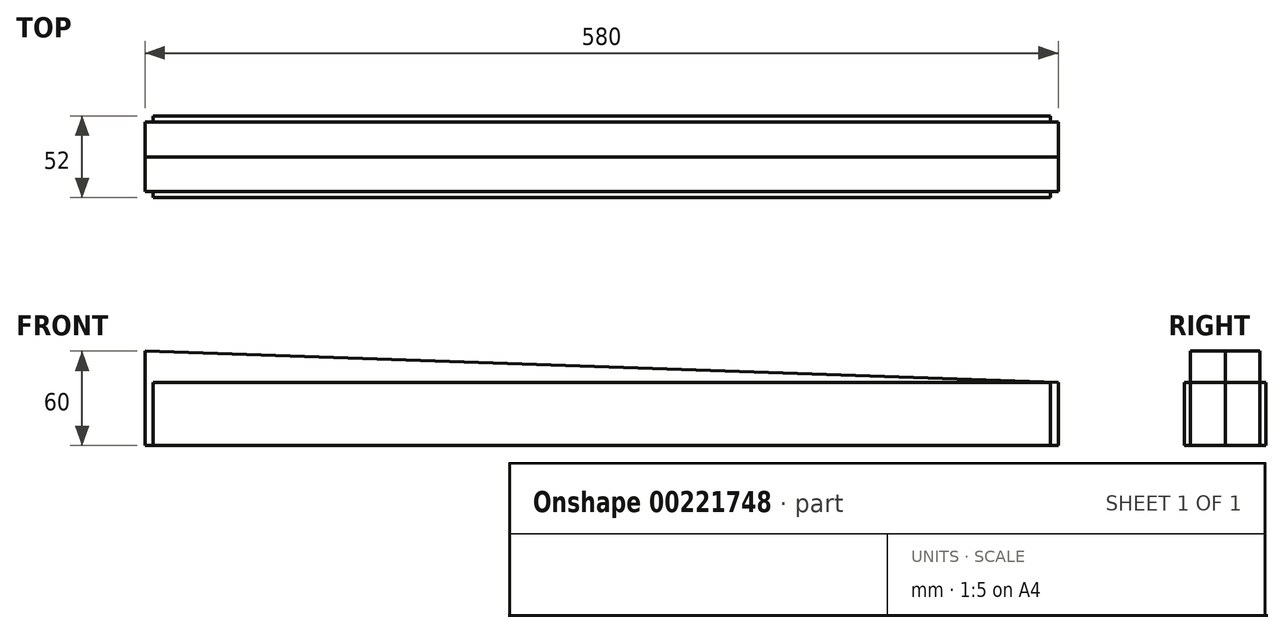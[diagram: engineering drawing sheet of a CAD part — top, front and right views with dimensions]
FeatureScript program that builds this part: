
annotation { "Feature Type Name" : "Feature", "Feature Type Description" : "" }
export const myFeature = defineFeature(function(context is Context, id is Id, definition is map)
    precondition{}
    {
        {
            var Q0;
            Q0=qCreatedBy(makeId("Front.planeOp"),FACE);
            var sketch = newSketch(context, id + "F0", { "sketchPlane" : qUnion([Q0])});
            skLineSegment(sketch, "E0.bottom", {"start": v(-290, 40) * mm, "end": v(290, 20) * mm});
            skLineSegment(sketch, "E0.top", {"start": v(-290, -20) * mm, "end": v(290, -20) * mm});
            skLineSegment(sketch, "E0.left", {"start": v(-290, 40) * mm, "end": v(-290, -20) * mm});
            skLineSegment(sketch, "E0.right", {"start": v(290, 20) * mm, "end": v(290, -20) * mm});
            skPoint(sketch, "E0.middle", {"position": v(0, 0) * mm});
            skSolve(sketch);
        }
        {
            var Q0;
            Q0 = qSketchRegion(id + "F0", true);
            extrude(context, id + "F1", {"entities" : qUnion([Q0]), "depth" : 22 * mm});
        }
        {
            var Q0;
            Q0=makeQuery(id+"F1.opExtrude","CAP_FACE",FACE,{"disambiguationData":[OSD([sQuery(id+"F0.wireOp",EDGE,"E0.bottom"),sQuery(id+"F0.wireOp",EDGE,"E0.top"),sQuery(id+"F0.wireOp",EDGE,"E0.left"),sQuery(id+"F0.wireOp",EDGE,"E0.right")])],"isStart":true});
            var sketch = newSketch(context, id + "F2", { "sketchPlane" : qUnion([Q0])});
            skLineSegment(sketch, "E1.0", {"start": v(290, -20) * mm, "end": v(-290, -20) * mm});
            skLineSegment(sketch, "E2", {"start": v(-285, -20) * mm, "end": v(-285, 20) * mm});
            skLineSegment(sketch, "E3", {"start": v(-285, 20) * mm, "end": v(285, 20) * mm});
            skLineSegment(sketch, "E4", {"start": v(285, 20) * mm, "end": v(285, -20) * mm});
            skSolve(sketch);
        }
        {
            var Q0;
            {var subQ0=sQuery(id+"F2.wireOp",EDGE,"E2");Q0=makeQuery(id+"F2.imprint","IMPRINT",FACE,{"disambiguationData":[TD([[makeQuery(id+"F2.imprint","IMPRINT",EDGE,{"derivedFrom":subQ0}),-1.0]])]});}
            extrude(context, id + "F3", {"entities" : qUnion([Q0]), "operationType" : NewBodyOperationType.ADD, "depth" : 4 * mm});
        }
        {
            var Q0;
            Q0=makeQuery(id+"F1.opExtrude","SWEPT_BODY",BODY,{"disambiguationData":[OSD([sQuery(id+"F0.wireOp",EDGE,"E0.bottom"),sQuery(id+"F0.wireOp",EDGE,"E0.top"),sQuery(id+"F0.wireOp",EDGE,"E0.left"),sQuery(id+"F0.wireOp",EDGE,"E0.right")])]});
            var Q1;
            Q1=makeQuery(id+"F1.opExtrude","CAP_FACE",FACE,{"disambiguationData":[OSD([sQuery(id+"F0.wireOp",EDGE,"E0.bottom"),sQuery(id+"F0.wireOp",EDGE,"E0.top"),sQuery(id+"F0.wireOp",EDGE,"E0.left"),sQuery(id+"F0.wireOp",EDGE,"E0.right")])],"isStart":false});
            mirror(context, id + "F4", {"entities" : qUnion([Q0]), "mirrorPlane" : qUnion([Q1])});
        }
    });
